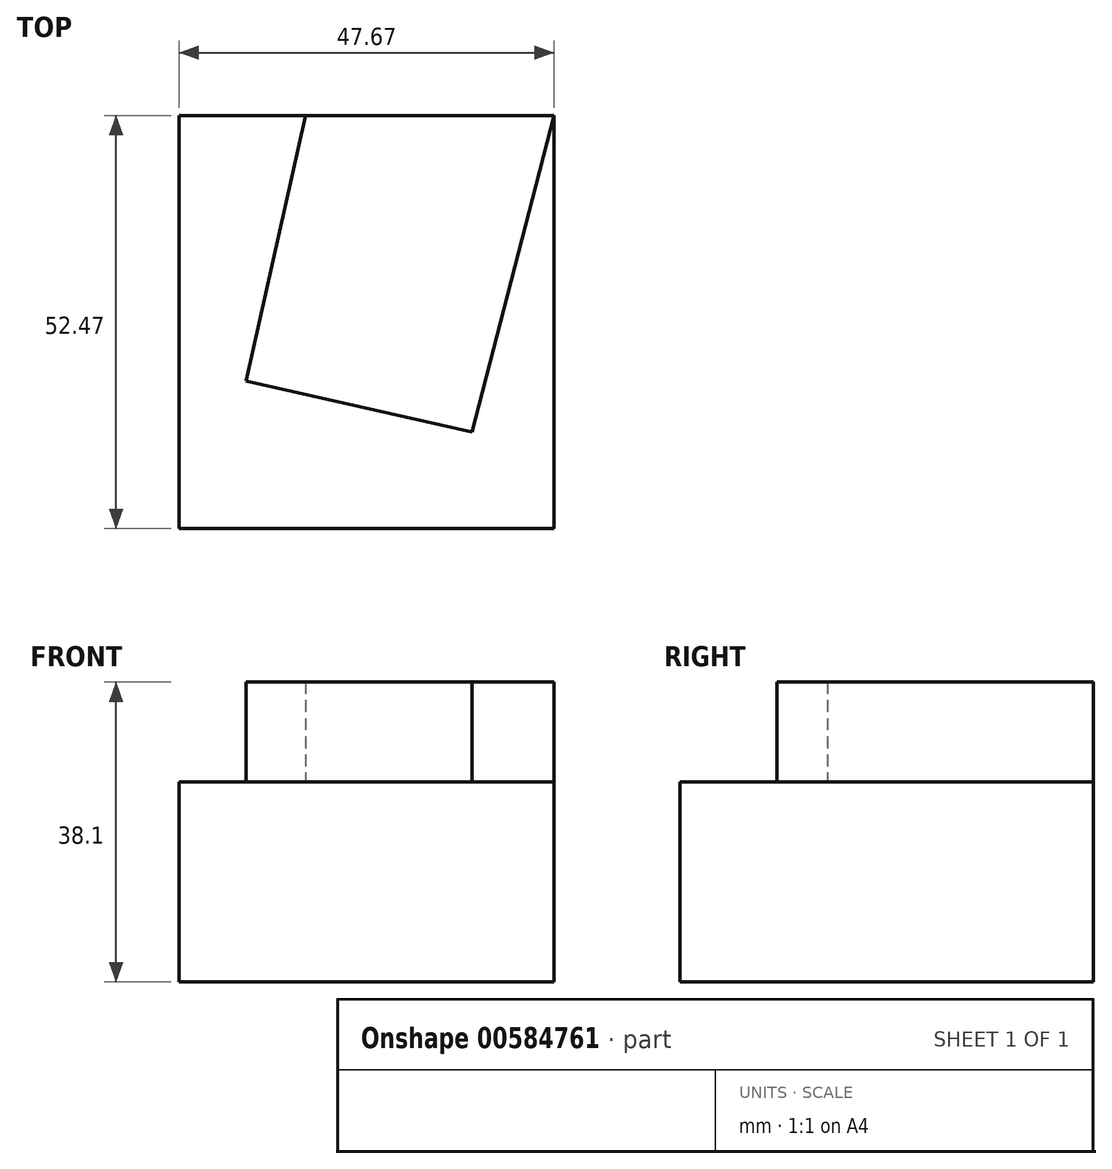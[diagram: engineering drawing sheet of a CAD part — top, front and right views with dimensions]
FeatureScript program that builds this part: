
annotation { "Feature Type Name" : "Feature", "Feature Type Description" : "" }
export const myFeature = defineFeature(function(context is Context, id is Id, definition is map)
    precondition{}
    {
        {
            var Q0;
            Q0=qCreatedBy(makeId("Top.planeOp"),FACE);
            var sketch = newSketch(context, id + "F0", { "sketchPlane" : qUnion([Q0])});
            skLineSegment(sketch, "E0.bottom", {"start": v(-47.67, -12.2) * mm, "end": v(0, -12.2) * mm});
            skLineSegment(sketch, "E0.top", {"start": v(-47.67, -64.67) * mm, "end": v(0, -64.67) * mm});
            skLineSegment(sketch, "E0.left", {"start": v(-47.67, -12.2) * mm, "end": v(-47.67, -64.67) * mm});
            skLineSegment(sketch, "E0.right", {"start": v(0, -12.2) * mm, "end": v(0, -64.67) * mm});
            skSolve(sketch);
        }
        {
            var Q0;
            Q0=makeQuery(id+"F0.imprint","IMPRINT",FACE,{"disambiguationData":[TD([[makeQuery(id+"F0.imprint","IMPRINT",EDGE,{"derivedFrom":sQuery(id+"F0.wireOp",EDGE,"E0.bottom")}),-1.0]])]});
            extrude(context, id + "F1", {"entities" : qUnion([Q0]), "depth" : 25.4 * mm, "offsetDistance" : 25.4 * mm});
        }
        {
            var Q0;
            Q0=makeQuery(id+"F1.opExtrude","CAP_FACE",FACE,{"disambiguationData":[OSD([sQuery(id+"F0.wireOp",EDGE,"E0.bottom"),sQuery(id+"F0.wireOp",EDGE,"E0.top"),sQuery(id+"F0.wireOp",EDGE,"E0.left"),sQuery(id+"F0.wireOp",EDGE,"E0.right")])],"isStart":false});
            var sketch = newSketch(context, id + "F2", { "sketchPlane" : qUnion([Q0])});
            skLineSegment(sketch, "E1", {"start": v(-31.57, -12.2) * mm, "end": v(-39.15, -45.95) * mm});
            skLineSegment(sketch, "E2", {"start": v(-39.15, -45.95) * mm, "end": v(-10.47, -52.38) * mm});
            skLineSegment(sketch, "E3", {"start": v(-10.47, -52.38) * mm, "end": v(0, -12.2) * mm});
            skLineSegment(sketch, "E4", {"start": v(0, -12.2) * mm, "end": v(-31.57, -12.2) * mm});
            skSolve(sketch);
        }
        {
            var Q0;
            Q0=makeQuery(id+"F2.imprint","IMPRINT",FACE,{"disambiguationData":[TD([[makeQuery(id+"F2.imprint","IMPRINT",EDGE,{"derivedFrom":sQuery(id+"F2.wireOp",EDGE,"E1")}),1.0]])]});
            var sketch = newSketch(context, id + "F3", { "sketchPlane" : qUnion([Q0])});
            skSolve(sketch);
        }
        {
            var Q0;
            Q0=makeQuery(id+"F3.imprint","IMPRINT",FACE,{"disambiguationData":[TD([[makeQuery(id+"F3.imprint","IMPRINT",EDGE,{"derivedFrom":makeQuery(id+"F2.imprint","IMPRINT",EDGE,{"derivedFrom":sQuery(id+"F2.wireOp",EDGE,"E1")})}),1.0]])]});
            extrude(context, id + "F4", {"entities" : qUnion([Q0]), "operationType" : NewBodyOperationType.ADD, "depth" : 12.7 * mm, "offsetDistance" : 25.4 * mm});
        }
    });
